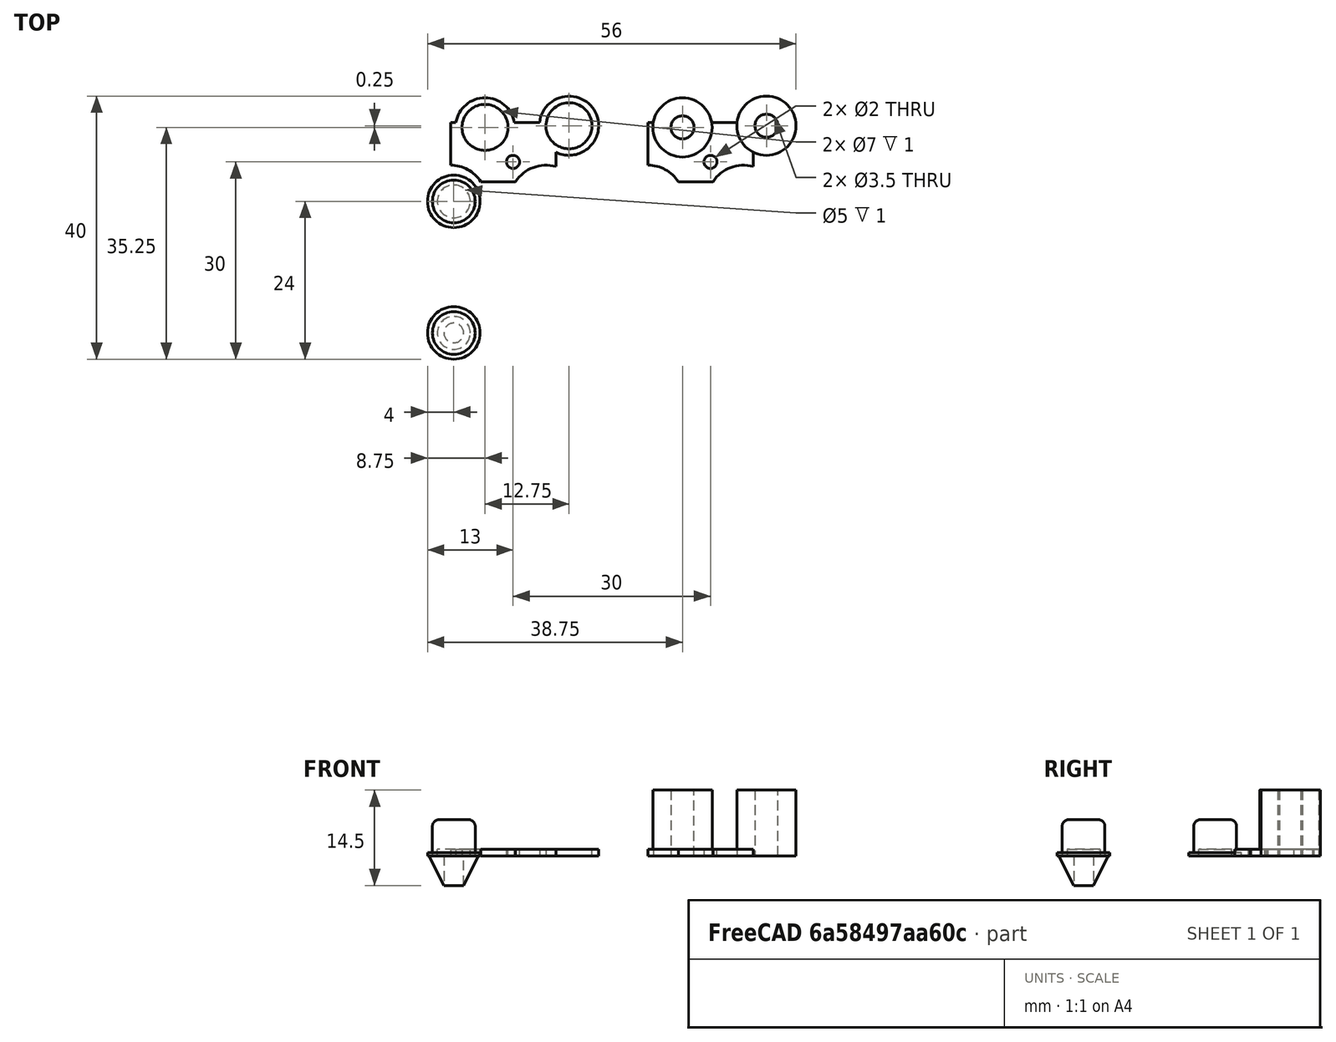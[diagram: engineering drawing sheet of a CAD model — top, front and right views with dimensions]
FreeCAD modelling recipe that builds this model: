
FCSTD DOCUMENT  (FreeCAD 1.0R38642 (Git))
Label: GBC_button_wells
License: All rights reserved
LicenseURL: http://en.wikipedia.org/wiki/All_rights_reserved
objects: Part::Cylinder×21, Part::MultiFuse×5, Part::Cut×3, Part::Box×2, Part::Fillet×2, Part::Cone×1
note: 34 computed .brp shape members not serialized (recipe doc carries the construction recipe); baked Part::Feature solids carry a one-line shape summary decoded from their .brp

FEATURE [Part::Cylinder] Cylinder  label="Cylinder(A)"
  Angle = 360
  AttacherType = Attacher::AttachEngine3D
  FirstAngle = 0
  Height = 10
  Placement = pos=(-0.5,0,0) rot=(0,0,1;0rad)
  Radius = 5.5
  SecondAngle = 0
FEATURE [Part::Cylinder] Cylinder001  label="Cylinder001(B)"
  Angle = 360
  AttacherType = Attacher::AttachEngine3D
  FirstAngle = 0
  Height = 10
  Placement = pos=(14,0,0) rot=(0,0,1;0rad)
  Radius = 5.5
  SecondAngle = 0
FEATURE [Part::Cylinder] Cylinder002  label="Cylinder002(post_hole)"
  Angle = 360
  AttacherType = Attacher::AttachEngine3D
  FirstAngle = 0
  Height = 10
  Placement = pos=(9,6,0) rot=(0,0,1;0rad)
  Radius = 1
  SecondAngle = 0
FEATURE [Part::Box] Box  label="Cube"
  AttacherType = Attacher::AttachEngine3D
  Height = 1
  Length = 16
  Placement = pos=(-0.5,3,0) rot=(0,0,1;0rad)
  Width = 9
FEATURE [Part::Cylinder] Cylinder003  label="Cylinder003(B2)(inner)"
  Angle = 360
  AttacherType = Attacher::AttachEngine3D
  FirstAngle = 0
  Height = 10
  Placement = pos=(17.5,11.5,0) rot=(0,0,1;0rad)
  Radius = 3.5
  SecondAngle = 0
FEATURE [Part::Cylinder] Cylinder004  label="Cylinder004(A2)(inner)"
  Angle = 360
  AttacherType = Attacher::AttachEngine3D
  FirstAngle = 0
  Height = 10
  Placement = pos=(4.75,11.25,0) rot=(0,0,1;0rad)
  Radius = 3.5
  SecondAngle = 0
FEATURE [Part::Cylinder] Cylinder005  label="Cylinder003(B2)(outer)"
  Angle = 360
  AttacherType = Attacher::AttachEngine3D
  FirstAngle = 0
  Height = 1
  Placement = pos=(17.5,11.5,0) rot=(0,0,1;0rad)
  Radius = 4.5
  SecondAngle = 0
FEATURE [Part::Cylinder] Cylinder006  label="Cylinder004(A2)(outer)"
  Angle = 360
  AttacherType = Attacher::AttachEngine3D
  FirstAngle = 0
  Height = 1
  Placement = pos=(4.75,11.25,0) rot=(0,0,1;0rad)
  Radius = 4.5
  SecondAngle = 0
FEATURE [Part::MultiFuse] Fusion
  Shapes = -> [Box,Cylinder005,Cylinder006]
FEATURE [Part::MultiFuse] Fusion001
  Shapes = -> [Cylinder,Cylinder002,Cylinder001,Cylinder003,Cylinder004]
FEATURE [Part::Cut] Cut  label="Cut(button_well)"
  Base = -> Fusion
  Tool = -> Fusion001
FEATURE [Part::Cylinder] Cylinder009  label="Cylinder008(button_rim)"
  Angle = 360
  AttacherType = Attacher::AttachEngine3D
  FirstAngle = 0
  Height = 0.5
  Radius = 4
  SecondAngle = 0
FEATURE [Part::Cylinder] Cylinder007  label="Cylinder(butotn_outer)"
  Angle = 360
  AttacherType = Attacher::AttachEngine3D
  FirstAngle = 0
  Height = 5.5
  Radius = 3.25
  SecondAngle = 0
FEATURE [Part::MultiFuse] Fusion002
  Shapes = -> [Cylinder009,Cylinder007]
FEATURE [Part::Cylinder] Cylinder008  label="Cylinder008(button_inner)"
  Angle = 360
  AttacherType = Attacher::AttachEngine3D
  FirstAngle = 0
  Height = 1
  Radius = 2.5
  SecondAngle = 0
FEATURE [Part::Cut] Cut003
  Base = -> Fusion002
  Tool = -> Cylinder008
FEATURE [Part::Fillet] Fillet  label="Fillet(button)"
  Base = -> Cut003
  EdgeLinks = -> Cut003 [Edge7]
  Edges = 1 edges r=1: [Edge7]
FEATURE [Part::Cylinder] Cylinder010  label="Cylinder002(post_hole)001"
  Angle = 360
  AttacherType = Attacher::AttachEngine3D
  FirstAngle = 0
  Height = 10
  Placement = pos=(9,6,0) rot=(0,0,1;0rad)
  Radius = 1
  SecondAngle = 0
FEATURE [Part::Cylinder] Cylinder011  label="Cylinder004(A2)(outer)001"
  Angle = 360
  AttacherType = Attacher::AttachEngine3D
  FirstAngle = 0
  Height = 10
  Placement = pos=(4.75,11.25,0) rot=(0,0,1;0rad)
  Radius = 4.5
  SecondAngle = 0
FEATURE [Part::Cylinder] Cylinder012  label="Cylinder003(B2)(inner)001"
  Angle = 360
  AttacherType = Attacher::AttachEngine3D
  FirstAngle = 0
  Height = 10
  Placement = pos=(17.5,11.5,0) rot=(0,0,1;0rad)
  Radius = 1.75
  SecondAngle = 0
FEATURE [Part::Cylinder] Cylinder013  label="Cylinder004(A2)(inner)001"
  Angle = 360
  AttacherType = Attacher::AttachEngine3D
  FirstAngle = 0
  Height = 10
  Placement = pos=(4.75,11.25,0) rot=(0,0,1;0rad)
  Radius = 1.75
  SecondAngle = 0
FEATURE [Part::Cylinder] Cylinder014  label="Cylinder(A)001"
  Angle = 360
  AttacherType = Attacher::AttachEngine3D
  FirstAngle = 0
  Height = 10
  Placement = pos=(-0.5,0,0) rot=(0,0,1;0rad)
  Radius = 5.5
  SecondAngle = 0
FEATURE [Part::Cylinder] Cylinder015  label="Cylinder003(B2)(outer)001"
  Angle = 360
  AttacherType = Attacher::AttachEngine3D
  FirstAngle = 0
  Height = 10
  Placement = pos=(17.5,11.5,0) rot=(0,0,1;0rad)
  Radius = 4.5
  SecondAngle = 0
FEATURE [Part::Cylinder] Cylinder016  label="Cylinder001(B)001"
  Angle = 360
  AttacherType = Attacher::AttachEngine3D
  FirstAngle = 0
  Height = 10
  Placement = pos=(14,0,0) rot=(0,0,1;0rad)
  Radius = 5.5
  SecondAngle = 0
FEATURE [Part::MultiFuse] Fusion003
  Shapes = -> [Cylinder014,Cylinder010,Cylinder016,Cylinder012,Cylinder013]
FEATURE [Part::Box] Box001  label="Cube001"
  AttacherType = Attacher::AttachEngine3D
  Height = 1
  Length = 16
  Placement = pos=(-0.5,3,0) rot=(0,0,1;0rad)
  Width = 9
FEATURE [Part::MultiFuse] Fusion004
  Shapes = -> [Box001,Cylinder015,Cylinder011]
FEATURE [Part::Cut] Cut004  label="Cut004(button_template)"
  Base = -> Fusion004
  Placement = pos=(30,0,0) rot=(0,0,1;0rad)
  Tool = -> Fusion003
FEATURE [Part::Cylinder] Cylinder017  label="Cylinder(clicky_button_outer)"
  Angle = 360
  AttacherType = Attacher::AttachEngine3D
  FirstAngle = 0
  Height = 5.5
  Placement = pos=(0,-20,0) rot=(0,0,1;0rad)
  Radius = 3.25
  SecondAngle = 0
FEATURE [Part::Cylinder] Cylinder018  label="Cylinder008(clicky_button_inner)"
  Angle = 360
  AttacherType = Attacher::AttachEngine3D
  FirstAngle = 0
  Height = 1
  Placement = pos=(0,-20,0) rot=(0,0,1;0rad)
  Radius = 2.5
  SecondAngle = 0
FEATURE [Part::Cylinder] Cylinder019  label="Cylinder008(clicky_button_rim)"
  Angle = 360
  AttacherType = Attacher::AttachEngine3D
  FirstAngle = 0
  Height = 0.5
  Placement = pos=(0,-20,0) rot=(0,0,1;0rad)
  Radius = 4
  SecondAngle = 0
FEATURE [Part::Cylinder] Cylinder020  label="Cylinder008(clicky_button_extender)"
  Angle = 360
  AttacherType = Attacher::AttachEngine3D
  FirstAngle = 0
  Height = 4.5
  Placement = pos=(0,-20,-4.5) rot=(0,0,1;0rad)
  Radius = 1.5
  SecondAngle = 0
FEATURE [Part::Cone] Cone
  Angle = 360
  AttacherType = Attacher::AttachEngine3D
  Height = 5
  Placement = pos=(0,-20,-4.5) rot=(0,0,1;0rad)
  Radius1 = 1.5
  Radius2 = 4
FEATURE [Part::Fillet] Fillet001
  Base = -> Cylinder017
  EdgeLinks = -> Cylinder017 [Edge3]
  Edges = 1 edges r=1: [Edge3]
